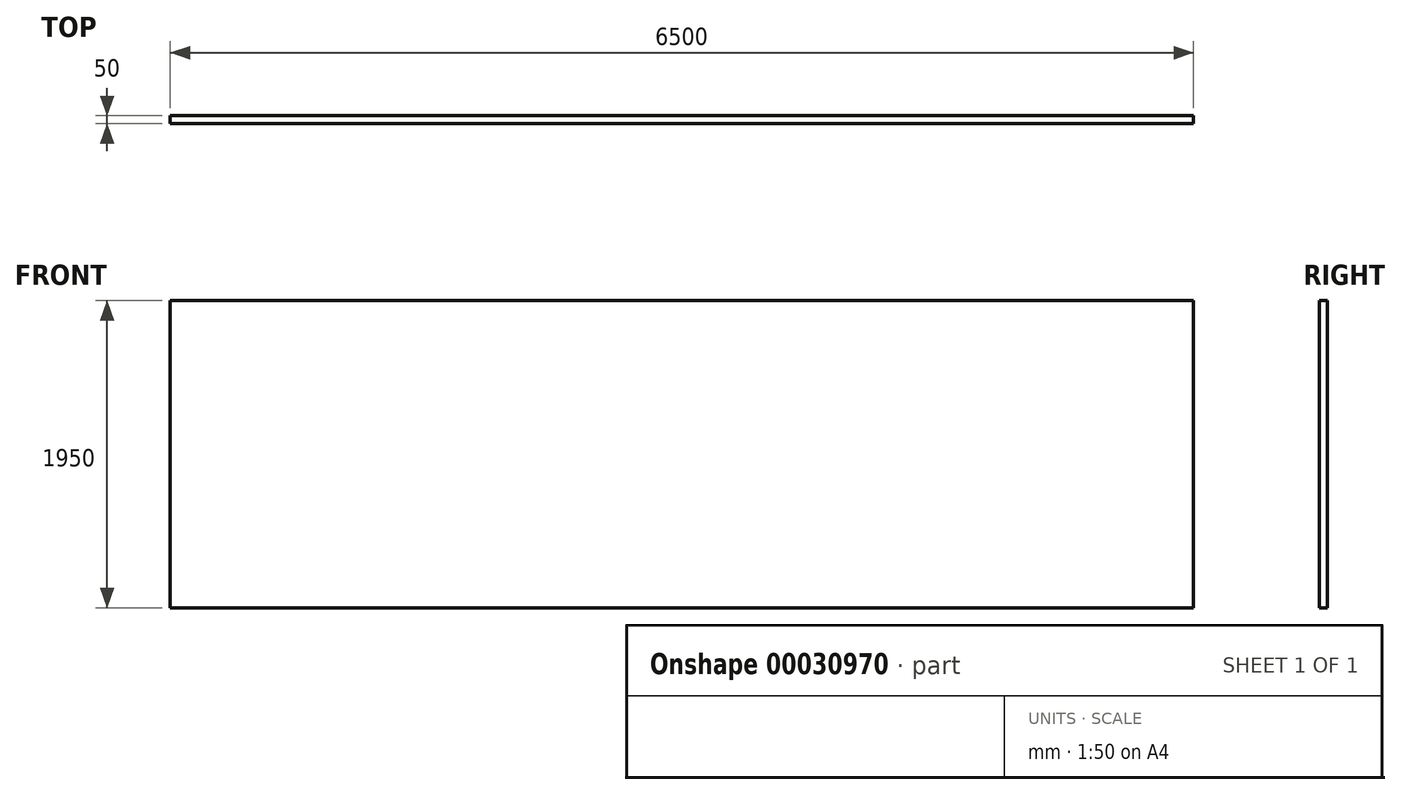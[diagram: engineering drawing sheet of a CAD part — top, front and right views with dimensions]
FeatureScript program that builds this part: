
annotation { "Feature Type Name" : "Feature", "Feature Type Description" : "" }
export const myFeature = defineFeature(function(context is Context, id is Id, definition is map)
    precondition{}
    {
        {
            var Q0;
            Q0=qCreatedBy(makeId("Front.planeOp"),FACE);
            var sketch = newSketch(context, id + "F0", { "sketchPlane" : qUnion([Q0])});
            skLineSegment(sketch, "E0.bottom", {"start": v(0, 0) * mm, "end": v(6500, 0) * mm});
            skLineSegment(sketch, "E0.top", {"start": v(0, 1950) * mm, "end": v(6500, 1950) * mm});
            skLineSegment(sketch, "E0.left", {"start": v(0, 0) * mm, "end": v(0, 1950) * mm});
            skLineSegment(sketch, "E0.right", {"start": v(6500, 0) * mm, "end": v(6500, 1950) * mm});
            skSolve(sketch);
        }
        {
            var Q0;
            Q0=makeQuery(id+"F0.imprint","IMPRINT",FACE,{"disambiguationData":[TD([[makeQuery(id+"F0.imprint","IMPRINT",EDGE,{"derivedFrom":sQuery(id+"F0.wireOp",EDGE,"E0.bottom")}),1.0]])]});
            extrude(context, id + "F1", {"entities" : qUnion([Q0]), "depth" : 50 * mm});
        }
    });
